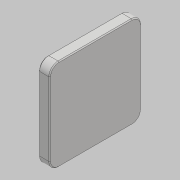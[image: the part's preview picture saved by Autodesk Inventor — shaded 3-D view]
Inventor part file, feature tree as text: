
AUTODESK INVENTOR PART (.ipt)
format: ipt  version: 2018 (Build 220112000, 112)  size: 100,864 bytes
history: native  units: mm
features: other x1, extrude x1, fillet x1, chamfer x1, sketch x1
ambient origin geometry x8: Origin, YZ Plane, XZ Plane, XY Plane, X Axis, Y Axis, Z Axis, Center Point
bodies: Body1 (feature_tree)
feature tree (5):
  other  "實體1"
  extrude  "擠出1"  Depth=100.0mm
  fillet  "圓角1"  Radius=100.0mm
  chamfer  "倒角1"  Distance=12.0mm
  sketch  "草圖1"
